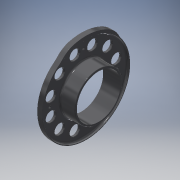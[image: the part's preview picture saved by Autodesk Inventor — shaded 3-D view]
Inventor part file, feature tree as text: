
AUTODESK INVENTOR PART (.ipt)
format: ipt  version: 2018 (Build 220112000, 112)  size: 301,056 bytes
history: native  units: mm
features: extrude x3, fillet x3, sketch x2, hole x2, chamfer x2, pattern_circular x2, other x1
ambient origin geometry x8: Origin, YZ Plane, XZ Plane, XY Plane, X Axis, Y Axis, Z Axis, Center Point
bodies: Solid1 (feature_tree)
feature tree (15):
  sketch  "Sketch1"  dims[d0=35.0mm d1=38.0mm]
  extrude  "Extrusion1"  Depth=38.0mm
  extrude  "Extrusion2"  Depth=0.1mm
  extrude  "Extrusion3"  Depth=0.1mm
  sketch  "Sketch2"  dims[d2=69.0mm d3=70.1mm d4=74.12mm d5=5.295329mm d6=6.675884mm d7=37.06mm d8=8.182104mm d9=5.506514mm d10=5.506514mm d11=1.507964mm d12=20.6mm d13=19.09mm d14=19.06mm d15=20.92mm d16=4.0mm d17=0.0mm d18=14.0mm d19=0.0mm d20=2.0mm d21=0.0mm d22=27.0mm d23=26.08mm d24=6.99mm d25=8.0mm d26=6.35mm d27=4.0mm d28=2.0mm d29=90.0deg d30=8.0mm d31=0.0mm d32=1.567mm d33=4.0mm d34=4.0mm d35=2.0mm d36=90.0deg d37=6.3mm d38=0.0mm d39=0.25mm d40=2.0mm d41=45.0deg d42=0.25mm d43=2.0mm d44=45.0deg d45=120.0mm d46=360.0deg d48=30.0mm d49=180.0deg d51=1.5mm d53=0.5mm d54=0.1mm]
  hole  "Hole1"  [1 undecoded]
  hole  "Hole2"  [1 undecoded]
  chamfer  "Chamfer1"  Distance=8.182104mm
  chamfer  "Chamfer2"  Distance=5.506514mm
  other  "Work Axis1"
  pattern_circular  "Circular Pattern1"  [2 undecoded]
  pattern_circular  "Circular Pattern2"  [2 undecoded]
  fillet  "Fillet1"  Radius=20.6mm
  fillet  "Fillet3"  Radius=19.09mm
  fillet  "Fillet4"  Radius=19.06mm
note: 6 required parameter values undecoded (feature->parameter linkage not recoverable at this tier; creation-order binding heuristic only, values carry confidence <= 0.55)
